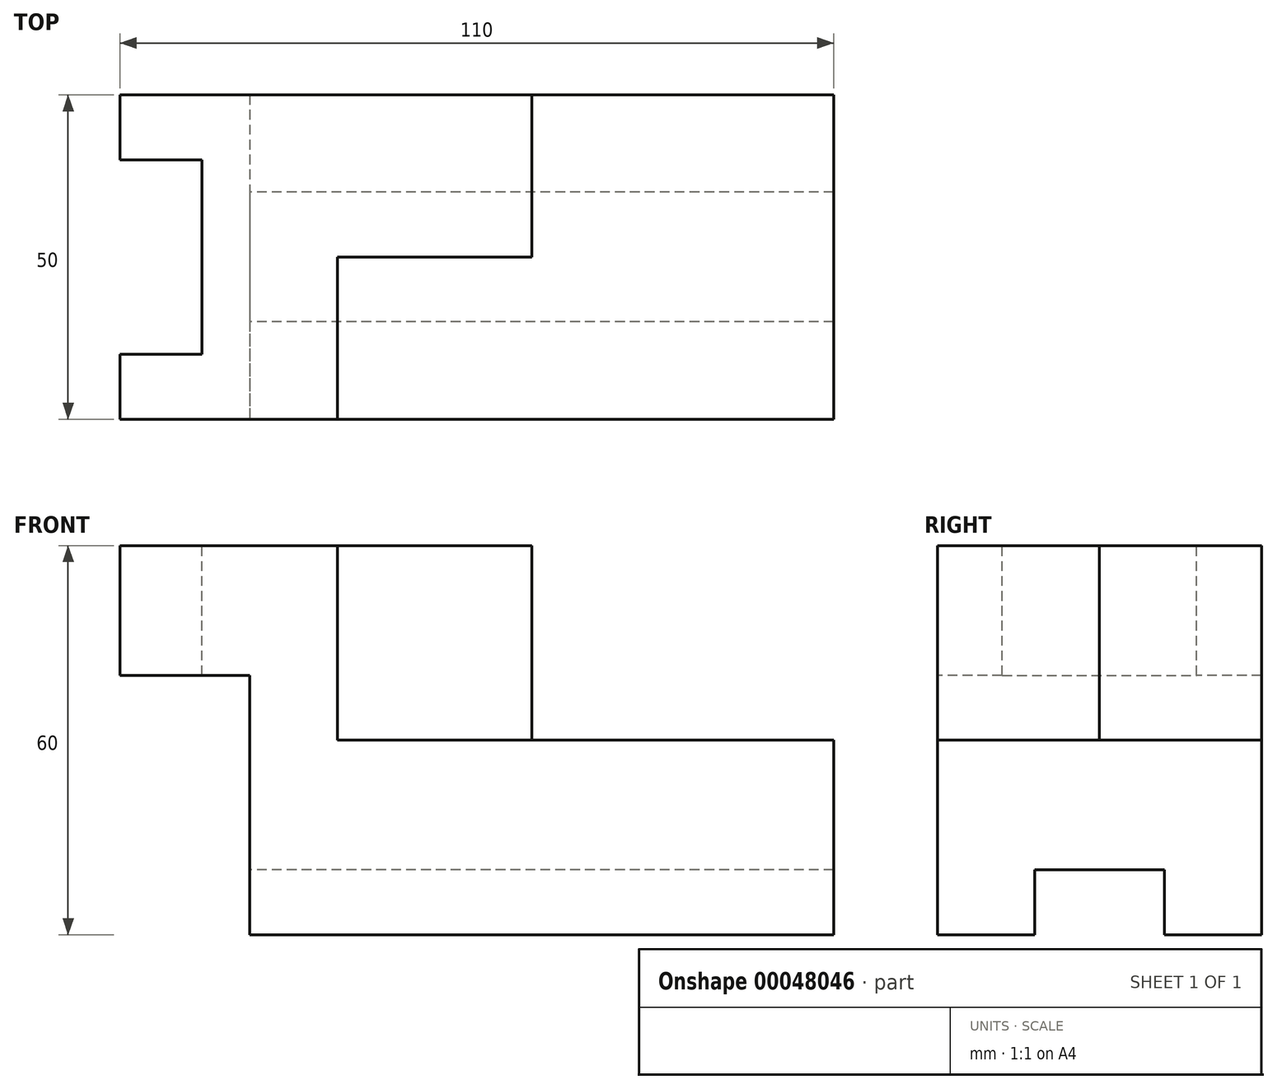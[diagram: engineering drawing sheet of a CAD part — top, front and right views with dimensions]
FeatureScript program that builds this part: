
annotation { "Feature Type Name" : "Feature", "Feature Type Description" : "" }
export const myFeature = defineFeature(function(context is Context, id is Id, definition is map)
    precondition{}
    {
        {
            assignVariable(context, id + "F0", {"name" : "C", "anyValue" : 50});
        }
        {
            var Q0;
            Q0=qCreatedBy(makeId("Front.planeOp"),FACE);
            var sketch = newSketch(context, id + "F1", { "sketchPlane" : qUnion([Q0])});
            skLineSegment(sketch, "E0", {"start": v(20, 0) * mm, "end": v(20, 40) * mm});
            skLineSegment(sketch, "E1", {"start": v(20, 40) * mm, "end": v(0, 40) * mm});
            skLineSegment(sketch, "E2", {"start": v(0, 40) * mm, "end": v(0, 60) * mm});
            skLineSegment(sketch, "E3", {"start": v(0, 60) * mm, "end": v(41.16, 60) * mm});
            skLineSegment(sketch, "E4", {"start": v(41.16, 60) * mm, "end": v(41.16, 30) * mm});
            skLineSegment(sketch, "E5", {"start": v(41.16, 30) * mm, "end": v(110, 30) * mm});
            skLineSegment(sketch, "E6", {"start": v(110, 30) * mm, "end": v(110, 0) * mm});
            skLineSegment(sketch, "E7", {"start": v(110, 0) * mm, "end": v(20, 0) * mm});
            skLineSegment(sketch, "E8", {"start": v(41.16, 60) * mm, "end": v(63.48, 60) * mm});
            skLineSegment(sketch, "E9", {"start": v(63.48, 60) * mm, "end": v(63.48, 30) * mm});
            skSolve(sketch);
        }
        {
            var Q0;
            Q0 = qSketchRegion(id + "F1", true);
            extrude(context, id + "F2", {"entities" : qUnion([Q0]), "oppositeDirection" : true, "depth" : (getVariable(context, 'C')) * mm});
        }
        {
            var Q0;
            Q0=makeQuery(id+"F2.opExtrude","SWEPT_FACE",FACE,{"disambiguationData":[OSD([sQuery(id+"F1.wireOp",EDGE,"E3"),sQuery(id+"F1.wireOp",EDGE,"E8")])]});
            var sketch = newSketch(context, id + "F3", { "sketchPlane" : qUnion([Q0])});
            skLineSegment(sketch, "E10.bottom", {"start": v(63.48, 0) * mm, "end": v(33.48, 0) * mm});
            skLineSegment(sketch, "E10.top", {"start": v(63.48, 25) * mm, "end": v(33.48, 25) * mm});
            skLineSegment(sketch, "E10.left", {"start": v(63.48, 0) * mm, "end": v(63.48, 25) * mm});
            skLineSegment(sketch, "E10.right", {"start": v(33.48, 0) * mm, "end": v(33.48, 25) * mm});
            skSolve(sketch);
        }
        {
            var Q0;
            Q0 = qSketchRegion(id + "F3", true);
            extrude(context, id + "F4", {"entities" : qUnion([Q0]), "operationType" : NewBodyOperationType.REMOVE, "oppositeDirection" : true, "depth" : 30 * mm});
        }
        {
            var Q0;
            Q0=makeQuery(id+"F2.opExtrude","SWEPT_FACE",FACE,{"disambiguationData":[OSD([sQuery(id+"F1.wireOp",EDGE,"E3"),sQuery(id+"F1.wireOp",EDGE,"E8")])]});
            var sketch = newSketch(context, id + "F5", { "sketchPlane" : qUnion([Q0])});
            skLineSegment(sketch, "E11.bottom", {"start": v(0, 10) * mm, "end": v(12.6, 10) * mm});
            skLineSegment(sketch, "E11.top", {"start": v(0, 40) * mm, "end": v(12.6, 40) * mm});
            skLineSegment(sketch, "E11.left", {"start": v(0, 10) * mm, "end": v(0, 40) * mm});
            skLineSegment(sketch, "E11.right", {"start": v(12.6, 10) * mm, "end": v(12.6, 40) * mm});
            skSolve(sketch);
        }
        {
            var Q0;
            Q0 = qSketchRegion(id + "F5", true);
            extrude(context, id + "F6", {"entities" : qUnion([Q0]), "operationType" : NewBodyOperationType.REMOVE, "oppositeDirection" : true, "depth" : 60 * mm});
        }
        {
            var Q0;
            Q0=makeQuery(id+"F2.opExtrude","SWEPT_FACE",FACE,{"disambiguationData":[OSD([sQuery(id+"F1.wireOp",EDGE,"E7")])]});
            var sketch = newSketch(context, id + "F7", { "sketchPlane" : qUnion([Q0])});
            skLineSegment(sketch, "E12.bottom", {"start": v(110, -15) * mm, "end": v(20, -15) * mm});
            skLineSegment(sketch, "E12.top", {"start": v(110, -35) * mm, "end": v(20, -35) * mm});
            skLineSegment(sketch, "E12.left", {"start": v(110, -15) * mm, "end": v(110, -35) * mm});
            skLineSegment(sketch, "E12.right", {"start": v(20, -15) * mm, "end": v(20, -35) * mm});
            skSolve(sketch);
        }
        {
            var Q0;
            Q0 = qSketchRegion(id + "F7", true);
            var Q1;
            Q1=makeQuery(id+"F7.imprint","IMPRINT",FACE,{"disambiguationData":[TD([[makeQuery(id+"F7.imprint","IMPRINT",EDGE,{"derivedFrom":sQuery(id+"F7.wireOp",EDGE,"E12.bottom")}),1.0]])]});
            extrude(context, id + "F8", {"entities" : qUnion([Q0, Q1]), "operationType" : NewBodyOperationType.REMOVE, "oppositeDirection" : true, "depth" : 10 * mm});
        }
    });
